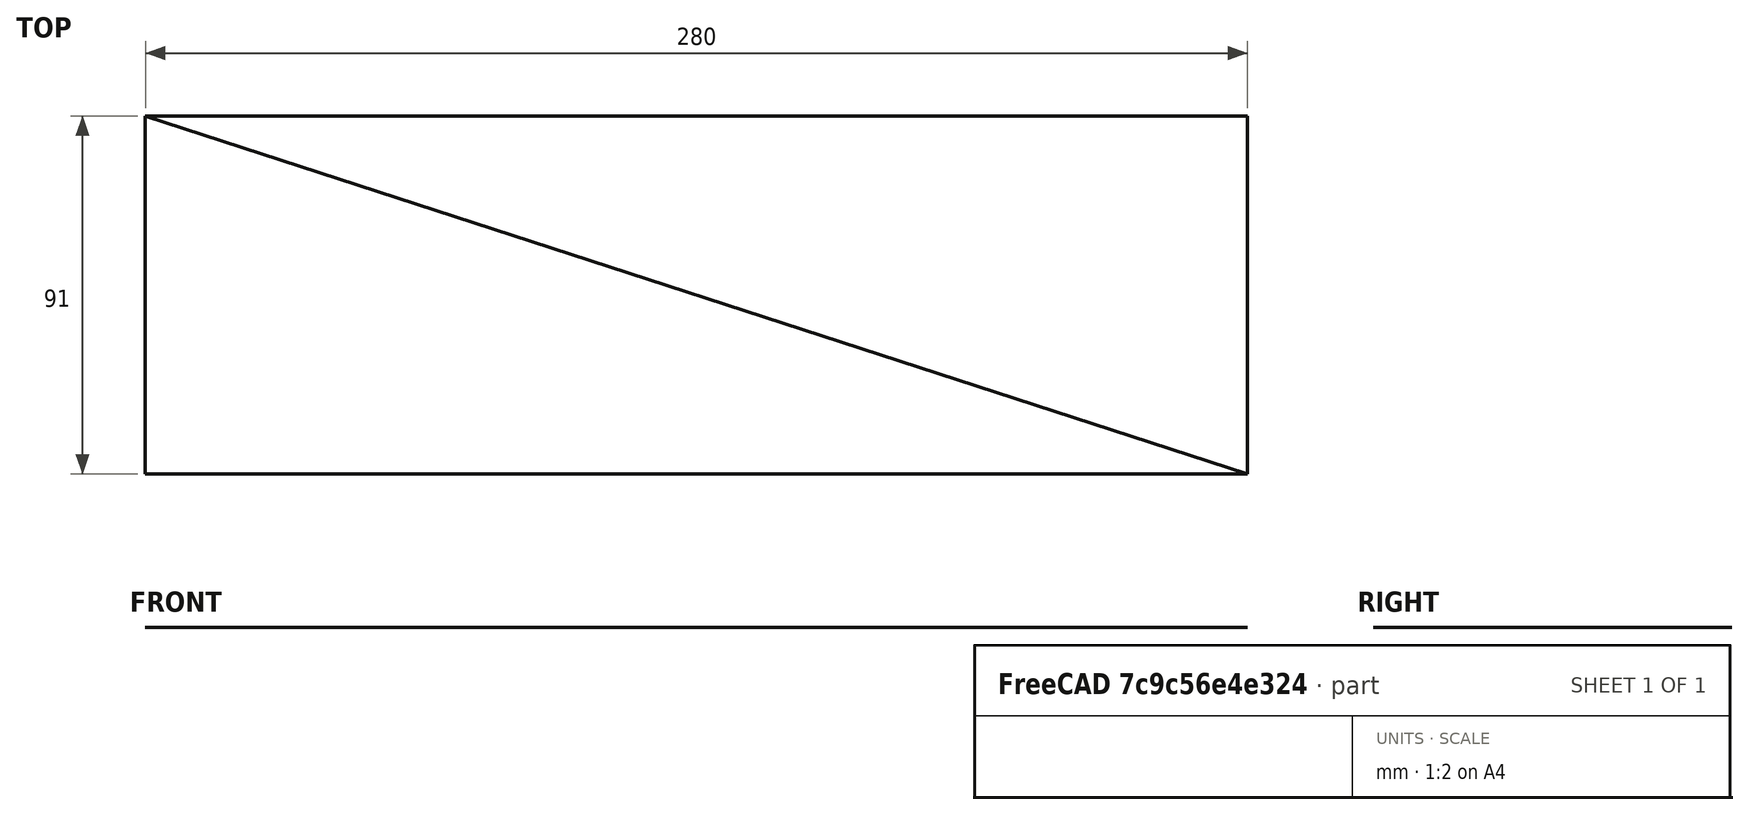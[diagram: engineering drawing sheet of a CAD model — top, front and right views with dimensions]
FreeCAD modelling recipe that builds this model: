
FCSTD DOCUMENT  (FreeCAD 1.1R20260325 (Git shallow))
Label: Caixa_Distribuicao_Embutir
License: All rights reserved
LicenseURL: http://en.wikipedia.org/wiki/All_rights_reserved
objects: Part::FeaturePython×1, Part::Feature×1, App::DocumentObjectGroup×1
note: 2 computed .brp shape members not serialized (recipe doc carries the construction recipe); baked Part::Feature solids carry a one-line shape summary decoded from their .brp

FEATURE [Part::FeaturePython] Component  label="Caixa_Distribuicao_Embutir"  # Arch/BIM 0 (typed FeaturePython)
  HorizontalArea = 0
  IfcData = attributes={"GlobalId": {"name": "GlobalId", "type": "IfcGloballyUniqueId", "is_enum": false, "enum_values": []}, "Description": {"... (+538 chars omitted),+1 more (map truncated)
  IfcType = 0
  MoveBase = false
  MoveWithHost = false
  PerimeterLength = 0
  Placement = pos=(0,0,1300) rot=(0,0,1;0rad)
  PredefinedType = 0
  VerticalArea = 0
FEATURE [Part::Feature] Compound002002002004005002002003003002003005002002005002002002002002002002002002002002002001  label="Simbologia_cx_distribuicao"
  Placement = pos=(-1519.58,92.2217,1561.71) rot=(0,0,1;0rad)
  shape: bbox 280 x 91 x 2e-07 mm, 1 faces, 0 solids (baked)
FEATURE [App::DocumentObjectGroup] Group  label="Caixa_Distribuicao_com_Simbologia"
  Group = -> [Compound002002002004005002002003003002003005002002005002002002002002002002002002002002002001,Component]
